# Revit family: Table-LAMMHULTS-COOPER-Round
name_source: partatom
category: Furniture
revit_build: Autodesk Revit 2015 (Build: 20160512_0715(x64)
units: mm (PartAtom-declared; Revit-internal decimal feet)

## types (12) — shared parameters
Assembly Code = E2020
Description = *Please enter mtrl description here for use in mto*
Frame Material = Metal - Chrome - Polished
Keynote = 46.B
Legs Material = Plastic - Black
Manufacturer = LAMMHULTS
Model = COOPER
Table Edge Material = <By Category>
URL = www.lammhults.se

## per-type parameters (varying)
| type | D120 | D90 | Diameter | Height | Table Top Height | Table Top Material |
| H45 D90 Laminate | No | Yes | 900 mm  [stored 2.95276 ft] | 450 mm  [stored 1.47638 ft] | 450 mm  [stored 1.47638 ft] | Laminate - High Pressure - White grey |
| H45 D90 Walnut Veneer | No | Yes | 900 mm  [stored 2.95276 ft] | 450 mm  [stored 1.47638 ft] | 450 mm  [stored 1.47638 ft] | Wood - Veneer - Walnut |
| H45 D120 Laminate | Yes | No | 1200 mm | 450 mm  [stored 1.47638 ft] | 450 mm  [stored 1.47638 ft] | Laminate - High Pressure - White grey |
| H45 D120 Walnut Veneer | Yes | No | 1200 mm | 450 mm  [stored 1.47638 ft] | 450 mm  [stored 1.47638 ft] | Wood - Veneer - Walnut |
| H52 D90 Laminate | No | Yes | 900 mm  [stored 2.95276 ft] | 520 mm  [stored 1.70604 ft] | 520 mm  [stored 1.70604 ft] | Laminate - High Pressure - White grey |
| H52 D90 Walnut Veneer | No | Yes | 900 mm  [stored 2.95276 ft] | 520 mm  [stored 1.70604 ft] | 520 mm  [stored 1.70604 ft] | Wood - Veneer - Walnut |
| H52 D120 Laminate | Yes | No | 1200 mm | 520 mm  [stored 1.70604 ft] | 520 mm  [stored 1.70604 ft] | Laminate - High Pressure - White grey |
| H52 D120 Walnut Veneer | Yes | No | 1200 mm | 520 mm  [stored 1.70604 ft] | 520 mm  [stored 1.70604 ft] | Wood - Veneer - Walnut |
| H72 D90 Laminate | No | Yes | 900 mm  [stored 2.95276 ft] | 720 mm  [stored 2.3622 ft] | 720 mm  [stored 2.3622 ft] | Laminate - High Pressure - White grey |
| H72 D90 Walnut Veneer | No | Yes | 900 mm  [stored 2.95276 ft] | 720 mm  [stored 2.3622 ft] | 720 mm  [stored 2.3622 ft] | Wood - Veneer - Walnut |
| H72 D120 Laminate | Yes | No | 1200 mm | 720 mm  [stored 2.3622 ft] | 720 mm  [stored 2.3622 ft] | Laminate - High Pressure - White grey |
| H72 D120 Walnut Veneer | Yes | No | 1200 mm | 720 mm  [stored 2.3622 ft] | 720 mm  [stored 2.3622 ft] | Wood - Veneer - Walnut |

note: [stored X ft] marks values corroborated as IEEE doubles in the binary element streams (Revit-internal decimal feet)

## geometry (parser evidence)
native form markers: Blend x12, Sweep x2
no freeform markers — native parametric forms only
